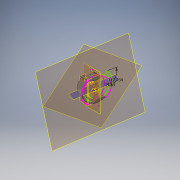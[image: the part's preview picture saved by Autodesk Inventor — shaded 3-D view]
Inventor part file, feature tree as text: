
AUTODESK INVENTOR PART (.ipt)
format: ipt  version: 2020 (Build 240168000, 168)  size: 554,496 bytes
history: native  units: mm
features: other x32, extrude x12, sketch x11, reference x7, projected_geometry x3, revolve x1, mirror x1
ambient origin geometry x8: Origin, YZ Plane, XZ Plane, XY Plane, X Axis, Y Axis, Z Axis, Center Point
bodies: Body1 (feature_tree)
feature tree (67):
  other  "Твердое тело1"
  other  "РабПлоскость26"
  sketch  "Эскиз2"
  other  "РабПлоскость21"
  sketch  "Эскиз5"
  other  "РабОсь1"
  revolve  "Вращение1"
  other  "РабПлоскость27"
  extrude  "Выдавливание1"  TaperAngle=90.0deg  [1 undecoded]
  other  "РабПлоскость5"
  other  "РабПлоскость9"
  other  "РабПлоскость11"
  sketch  "Эскиз7"
  other  "РабТочка9"
  extrude  "Выдавливание3"  Depth=10.0mm TaperAngle=0.0deg
  other  "РабПлоскость22"
  extrude  "Выдавливание4"  Depth=2.5mm
  other  "РабОсь2"
  other  "РабПлоскость23"
  extrude  "Выдавливание6"  Depth=2.0mm
  other  "РабПлоскость24"
  sketch  "Эскиз11"
  other  "РабПлоскость25"
  other  "РабПлоскость13"
  other  "РабПлоскость14"
  extrude  "Выдавливание7"  Depth=3.0mm
  extrude  "Выдавливание8"  Depth=10.0mm TaperAngle=0.0deg
  other  "РабПлоскость15"
  other  "РабПлоскость16"
  extrude  "Выдавливание9"  Depth=10.0mm TaperAngle=0.0deg
  other  "РабПлоскость17"
  extrude  "Выдавливание10"  Depth=7.0mm
  other  "РабПлоскость18"
  sketch  "Эскиз17"
  other  "РабПлоскость19"
  extrude  "Выдавливание11"  Depth=0.4mm
  extrude  "Выдавливание12"  Depth=10.0mm TaperAngle=0.0deg
  mirror  "Зеркальное отражение2"
  extrude  "Выдавливание13"  Depth=10.0mm TaperAngle=0.0deg
  extrude  "Выдавливание14"  TaperAngle=0.0deg  [1 undecoded]
  other  "РабПлоскость20"
  sketch  "Эскиз22"
  other  "РабОсь3"
  sketch  "Эскиз6"
  projected_geometry  "Спроецированная петля1"
  sketch  "Эскиз8"
  sketch  "Эскиз15"
  reference  "Ссылка15"
  reference  "Ссылка16"
  sketch  "Эскиз16"
  reference  "Ссылка17"
  reference  "Ссылка18"
  reference  "Ссылка20"
  reference  "Ссылка21"
  reference  "Ссылка22"
  sketch  "Эскиз18"
  projected_geometry  "Спроецированная петля3"
  projected_geometry  "Спроецированная петля4"
  parser-record x1  (decoder bookkeeping rows leaked as tree rows — omitted from the tree; the rows remain in map.json)
  other  "Omni_platform.iam"
  other  "SparkFun 9DoF Razor IMU:1"
  other  "MEGA 2560 PRO (EMBED):1"
  other  "Mega 2560 Pro - Board"
  other  "USB - Micro"
  other  "motherBoard_stend:1"
  other  "Board1.2:2"
  other  "floor:1"
note: 2 required parameter values undecoded (feature->parameter linkage not recoverable at this tier; creation-order binding heuristic only, values carry confidence <= 0.55)
note: 1 file-system path scrubbed to <path> (originals preserved in map.json)
